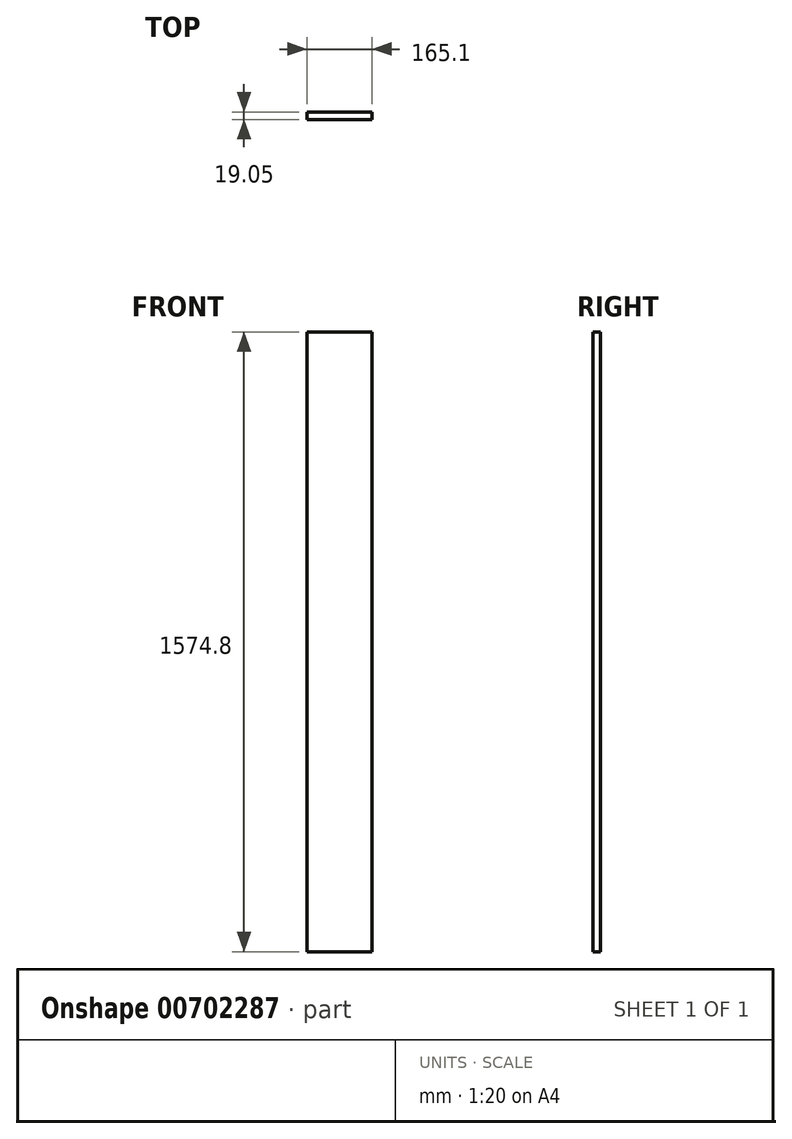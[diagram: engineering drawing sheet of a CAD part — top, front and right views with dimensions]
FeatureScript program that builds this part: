
annotation { "Feature Type Name" : "Feature", "Feature Type Description" : "" }
export const myFeature = defineFeature(function(context is Context, id is Id, definition is map)
    precondition{}
    {
        {
            var Q0;
            Q0=qCreatedBy(makeId("Front.planeOp"),FACE);
            var sketch = newSketch(context, id + "F0", { "sketchPlane" : qUnion([Q0])});
            skLineSegment(sketch, "E0.bottom", {"start": v(8.47, -42.62) * mm, "end": v(173.57, -42.62) * mm});
            skLineSegment(sketch, "E0.top", {"start": v(8.47, 1532.18) * mm, "end": v(173.57, 1532.18) * mm});
            skLineSegment(sketch, "E0.left", {"start": v(8.47, -42.62) * mm, "end": v(8.47, 1532.18) * mm});
            skLineSegment(sketch, "E0.right", {"start": v(173.57, -42.62) * mm, "end": v(173.57, 1532.18) * mm});
            skSolve(sketch);
        }
        {
            var Q0;
            Q0=makeQuery(id+"F0.imprint","IMPRINT",FACE,{"disambiguationData":[TD([[makeQuery(id+"F0.imprint","IMPRINT",EDGE,{"derivedFrom":sQuery(id+"F0.wireOp",EDGE,"E0.bottom")}),1.0]])]});
            var Q1;
            Q1 = qSketchRegion(id + "F0", true);
            extrude(context, id + "F1", {"entities" : qUnion([Q0, Q1]), "depth" : 19.05 * mm, "offsetDistance" : 25.4 * mm});
        }
        {
            var Q0;
            Q0=makeQuery(id+"F1.opExtrude","SWEPT_BODY",BODY,{"disambiguationData":[OSD([sQuery(id+"F0.wireOp",EDGE,"E0.bottom"),sQuery(id+"F0.wireOp",EDGE,"E0.top"),sQuery(id+"F0.wireOp",EDGE,"E0.left"),sQuery(id+"F0.wireOp",EDGE,"E0.right")])]});
            transform(context, id + "F2", {"entities" : qUnion([Q0]), "transformType" : TransformType.COPY});
        }
    });
